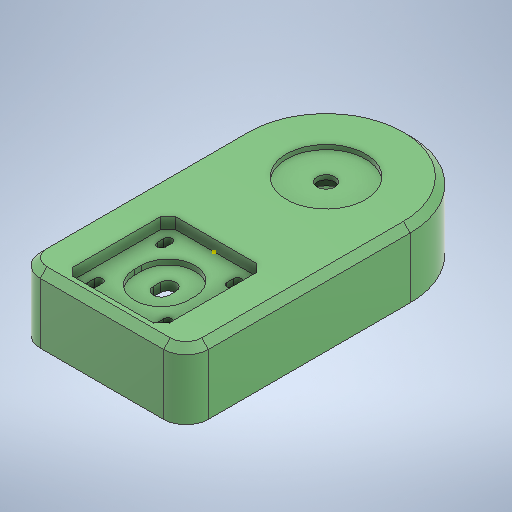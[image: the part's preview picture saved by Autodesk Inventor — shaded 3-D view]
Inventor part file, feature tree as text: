
AUTODESK INVENTOR PART (.ipt)
format: ipt  version: 2025.2 (Build 292293000, 293)  size: 389,120 bytes
history: native  units: mm
features: extrude x7, sketch x6, chamfer x2, fillet x1, shell x1
ambient origin geometry x8: Origin, YZ Plane, XZ Plane, XY Plane, X Axis, Y Axis, Z Axis, Center Point
bodies: Solid1 (feature_tree)
feature tree (17):
  extrude  "General shape"  Depth=75.0mm
  sketch  "Sketch2"  dims[d4=100.0mm d6=5.0mm d7=0.0mm]
  extrude  "Stepper recess face"  Depth=5.0mm TaperAngle=0.0deg
  extrude  "Stepper recess face hole"  Depth=2.3mm TaperAngle=0.0deg
  chamfer  "Stepper corners"  Distance=45.0mm
  fillet  "Rounded corners of the body"  Radius=7.0mm
  shell  "Shell1"  Thickness=8.0mm
  extrude  "Stepper mounting hole and shaft"  Depth=2.0mm
  extrude  "Slot for 608 bearing"  Depth=5.0mm TaperAngle=0.0deg
  sketch  "Sketch9"  dims[d17=4.0mm]
  extrude  "Extrusion11"  Depth=12.0mm
  sketch  "Sketch10"  dims[d18=1.8mm]
  extrude  "Extrusion13"  Depth=31.0mm
  chamfer  "Chamfer3"  Distance=31.0mm
  sketch  "Sketch1"  dims[d0=30.0mm d1=0.0mm d2=75.0mm]
  sketch  "Sketch6"  dims[d10=2.3mm d11=0.0mm d12=2.3mm d13=0.0mm]
  sketch  "Sketch11"  dims[d20=3.0mm d29=45.0mm d30=7.0mm d31=0.0mm d39=8.0mm d40=35.0mm d43=5.0mm d44=0.0mm d45=12.0mm d48=31.0mm d49=31.0mm d50=43.0mm d51=46.0mm d52=5.0mm d53=3.5mm d58=22.0mm d59=40.0mm d64=35.3mm d65=2.0mm d66=0.0mm d67=10.0mm d68=3.5mm d69=2.0mm d70=45.0deg d71=3.0mm d72=2.0mm d73=45.0deg d46=0.872665mm d47=0.5mm]
